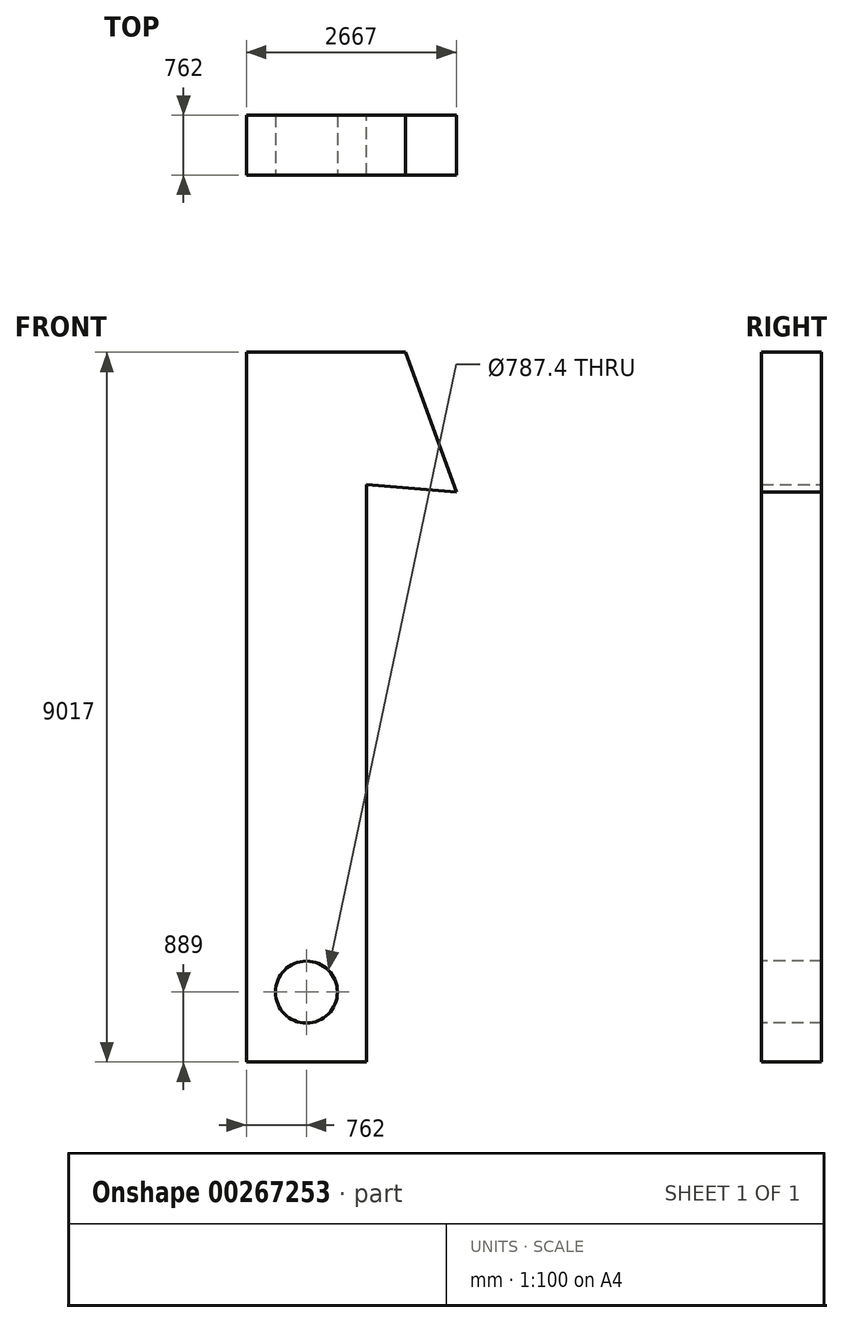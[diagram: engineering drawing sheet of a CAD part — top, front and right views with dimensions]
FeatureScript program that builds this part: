
annotation { "Feature Type Name" : "Feature", "Feature Type Description" : "" }
export const myFeature = defineFeature(function(context is Context, id is Id, definition is map)
    precondition{}
    {
        {
            var Q0;
            Q0=qCreatedBy(makeId("Front.planeOp"),FACE);
            var sketch = newSketch(context, id + "F0", { "sketchPlane" : qUnion([Q0])});
            skLineSegment(sketch, "E0", {"start": v(0, 0) * mm, "end": v(1524, 0) * mm});
            skLineSegment(sketch, "E1", {"start": v(1524, 0) * mm, "end": v(1524, 7339) * mm});
            skLineSegment(sketch, "E2", {"start": v(1524, 7339) * mm, "end": v(2667, 7239) * mm});
            skLineSegment(sketch, "E3", {"start": v(2667, 7239) * mm, "end": v(2019.86, 9017) * mm});
            skLineSegment(sketch, "E4", {"start": v(2019.86, 9017) * mm, "end": v(0, 9017) * mm});
            skLineSegment(sketch, "E5", {"start": v(0, 9017) * mm, "end": v(0, 0) * mm});
            skSolve(sketch);
        }
        {
            var Q0;
            Q0 = qSketchRegion(id + "F0", true);
            extrude(context, id + "F1", {"entities" : qUnion([Q0]), "depth" : 762 * mm});
        }
        {
            var Q0;
            Q0=makeQuery(id+"F1.opExtrude","CAP_FACE",FACE,{"disambiguationData":[OSD([sQuery(id+"F0.wireOp",EDGE,"E0"),sQuery(id+"F0.wireOp",EDGE,"E1"),sQuery(id+"F0.wireOp",EDGE,"E2"),sQuery(id+"F0.wireOp",EDGE,"E3"),sQuery(id+"F0.wireOp",EDGE,"E4"),sQuery(id+"F0.wireOp",EDGE,"E5")])],"isStart":false});
            var sketch = newSketch(context, id + "F2", { "sketchPlane" : qUnion([Q0])});
            skCircle(sketch, "E6", {"center": v(762, 889) * mm, "radius": 393.7 * mm});
            skSolve(sketch);
        }
        {
            var Q0;
            Q0 = qSketchRegion(id + "F2", true);
            extrude(context, id + "F3", {"entities" : qUnion([Q0]), "operationType" : NewBodyOperationType.REMOVE, "oppositeDirection" : true, "depth" : 1016 * mm});
        }
    });
